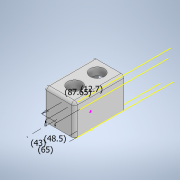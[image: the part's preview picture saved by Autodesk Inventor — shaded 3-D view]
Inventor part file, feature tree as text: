
AUTODESK INVENTOR PART (.ipt)
format: ipt  version: 2021 (Build 250183000, 183)  size: 219,136 bytes
history: native  units: in
note: dims shown in document units (in); Inventor stores cm internally (conversion verified against a paired STEP export)
features: extrude x5, sketch x5, fillet x3, other x2, imported_body x1
ambient origin geometry x8: Origin, YZ Plane, XZ Plane, XY Plane, X Axis, Y Axis, Z Axis, Center Point
bodies: Body1 (feature_tree)
feature tree (16):
  extrude  "Extrusion2"  Depth=2.5591in
  extrude  "Extrusion3"  Depth=2.5591in
  extrude  "Extrusion4"  Depth=1.3386in
  sketch  "Sketch6"  dims[d6=8.2677in d7=2.5591in]
  fillet  "Fillet1"  Radius=1.3386in
  extrude  "Extrusion5"  Depth=1.8898in
  fillet  "Fillet2"  Radius=1.8898in
  sketch  "Sketch8"  dims[d11=1.3386in d12=1.3386in d13=1.3386in]
  fillet  "Fillet3"  Radius=0.7087in
  sketch  "Sketch9"  dims[d14=1.8898in d15=1.8898in d16=1.8898in d19=0.7087in d20=0.0in]
  extrude  "Extrusion7"  Depth=0.4331in
  imported_body  "Base"
  other  "Top"
  other  "Walls"
  sketch  "Sketch7"  dims[d8=2.5591in d9=0.0in d10=1.3386in]
  sketch  "Sketch11"  dims[d21=0.4331in d22=0.4331in d23=0.4331in d24=0.4331in d25=1.9094in d26=0.0in d27=1.1811in d28=1.1811in d29=1.1811in d30=1.1811in d31=0.9449in d32=4.1339in d33=1.6929in d34=1.9094in d35=1.2992in d36=0.2362in d38=0.3937in d39=0.0in d40=0.5in d41=0.2362in d42=2.5591in d43=0.0591in d44=1.6929in d45=0.5in d46=3.4508in d47=2.5591in d50=4.1339in d51=0.0in]
